# Revit family: Hager-VOLTA-Hollow_wall-IP30-With_Cover-Without_DIN-Hosted-SE-en
name_source: partatom
category: Electrical Equipment
units: mm (PartAtom-declared; Revit-internal decimal feet)

## family parameters
Cut with Voids When Loaded = No
Host = Face
Maintain Annotation Orientation = Yes
Panel Configuration = Two Columns, Circuits Across
Part Type = Panelboard
Room Calculation Point = No
Round Connector Dimension = Use Diameter
Shared = No

## types (6) — shared parameters
BC_MODEL_ID = 1547281
BC_OBJECT_ID = 513510
BC_OBJECT_VERSION = #1
Code hager = ADD-EC000214_EU
EF000003 - Mounting method = Hollow wall
EF000007 - Colour = White
EF000008 - Width = 348 mm  [stored 1.14173 ft]
EF000024 - UV resistant = No
EF000049 - Depth = 98 mm  [stored 0.321522 ft]
EF000116 - RAL-number = 9010
EF000118 - With mounting plate = Yes
EF000218 - Built-in depth = 89 mm  [stored 0.291995 ft]
EF000846 - Built-in width = 315 mm
EF001062 - EMC-version = No
EF001088 - Extension possible = Yes
EF001134 - DIN-rail = No
EF002950 - Width in number of modular spacings = 12
EF004462 - Type of closure = Other
EF005474 - Degree of protection (IP) = IP30
EF006244 - Transparent cover/door = No
EF006306 - With lock = No
EF009212 - Cover model = With notch
EF015776 - Earthing terminal block = No
EF015777 - Neutral terminal block = No
ETIM class code = EC000214
ETIM class name = Small distribution board
HG000002-With door or cover = Yes
HG000003-Range = VOLTA
HG000005-Thickness = 2 mm  [stored 0.00656168 ft]
HG000006-Flush mounted = Yes
HG000009-Double swing door = No
HG000010-Asymmetric doors = No
HG000011-Empty rows from bottom = No
HG000012-Door swing angle = 90.00°
HG000013-Door on the left = No
HG000014-Door on the right = Yes
HG000015-Clearance visibility = Yes
HG000016-Door 3D visibility = Yes
HG000017-Distance between poles = 18 mm  [stored 0.0590551 ft]
HG000060-RAL-number = 9010
HG000099-Onfly Template ID = 507532
HGEF002950-Width in number of modular spacings = 12
Manufacturer = Hager
Name = VOLTA-Hollow_wall-IP30-With_Cover-Without_DIN-SE
Name BIM&CO = Electricity
Name hager = ADD_Enclosures_EC000214
Uniformat = Low Tension Service & Dist.
Uniformat code = D501001
zero-valued in all types: Default Elevation, EF000266 - Number of rows, EF001131 - Inner depth, HG000001-Number of columns, HG000007-Number of empty columns, HG000008-Number of empty rows, HGEF000266-Number of rows

## per-type parameters (varying)
| type | BC_VARIANT_ID | EF000040 - Height | EF000332 - Built-in height | EF015941 - Signal passing door | HG000004-Manufacturer reference |
| VOLTA-Hollow_wall_W348_H630_D98_12_Modular_Spacing-VH36NW | 1174439 | 630 mm  [stored 2.06693 ft] | 595 mm  [stored 1.9521 ft] | No | VH36NW |
| VOLTA-Hollow_wall_W348_H630_D98_12_Modular_Spacing-VH36WWH | 1174440 | 630 mm  [stored 2.06693 ft] | 595 mm  [stored 1.9521 ft] | Yes | VH36WWH |
| VOLTA-Hollow_wall_W348_H755_D98_12_Modular_Spacing-VH48NW | 1174441 | 755 mm  [stored 2.47703 ft] | 720 mm  [stored 2.3622 ft] | No | VH48NW |
| VOLTA-Hollow_wall_W348_H755_D98_12_Modular_Spacing-VH48WWH | 1174442 | 755 mm  [stored 2.47703 ft] | 720 mm  [stored 2.3622 ft] | Yes | VH48WWH |
| VOLTA-Hollow_wall_W348_H880_D98_12_Modular_Spacing-VH60NW | 1174444 | 880 mm  [stored 2.88714 ft] | 845 mm  [stored 2.77231 ft] | No | VH60NW |
| VOLTA-Hollow_wall_W348_H880_D98_12_Modular_Spacing-VH60WWH | 1174445 | 880 mm  [stored 2.88714 ft] | 845 mm  [stored 2.77231 ft] | Yes | VH60WWH |

note: column(s) folded — value = type name in every type: Reference

note: [stored X ft] marks values corroborated as IEEE doubles in the binary element streams (Revit-internal decimal feet)

## geometry (parser evidence)
native form markers: Sweep x14
no freeform markers — native parametric forms only
